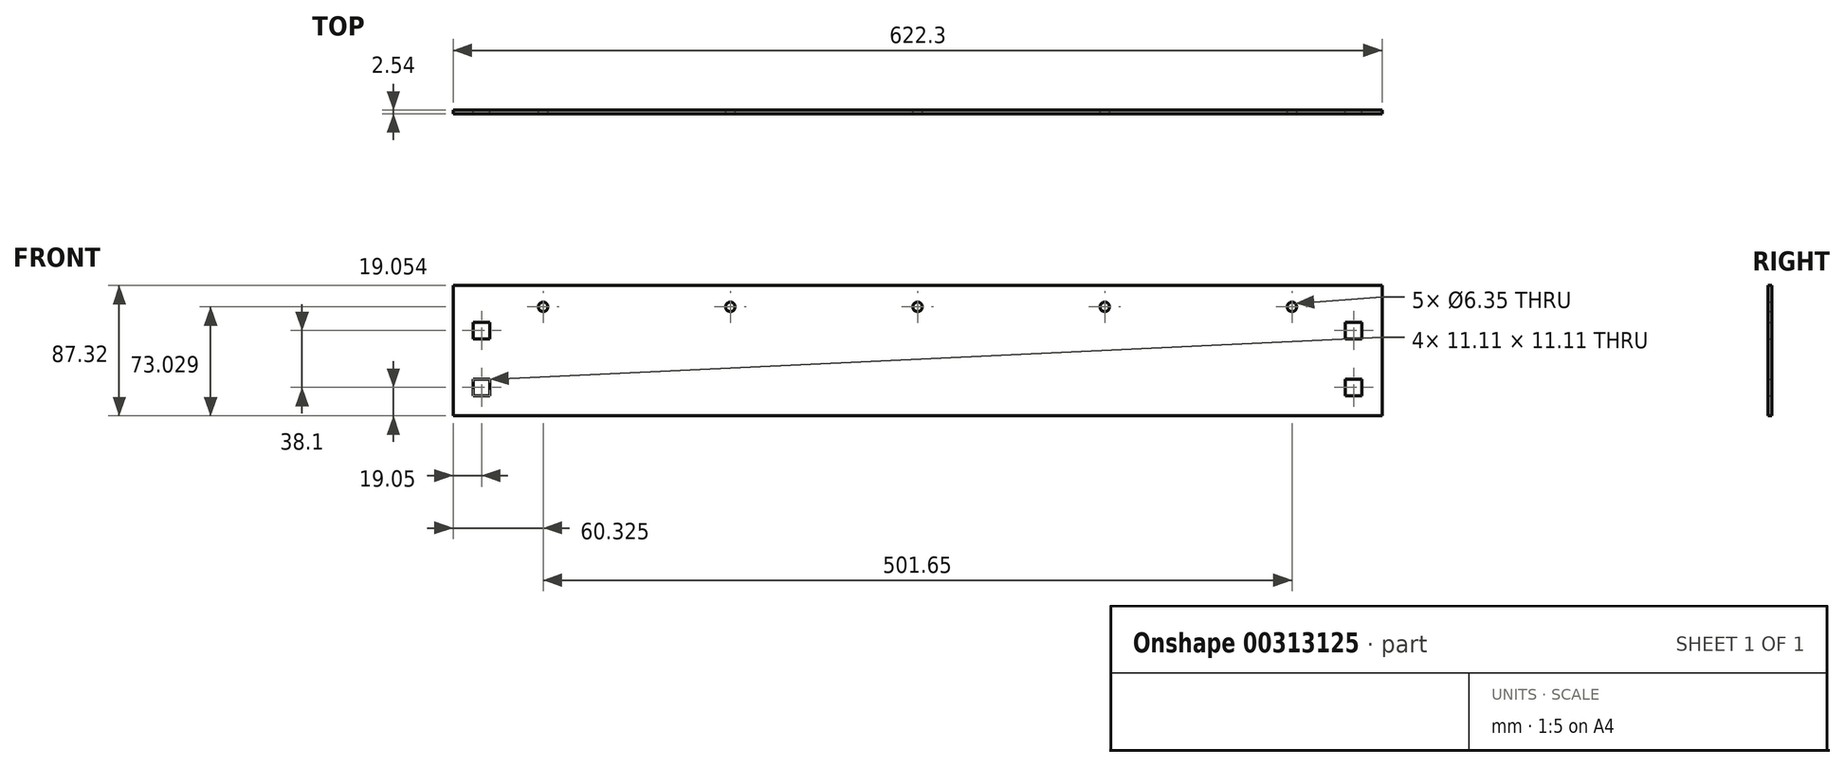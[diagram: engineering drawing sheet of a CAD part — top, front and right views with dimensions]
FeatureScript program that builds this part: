
annotation { "Feature Type Name" : "Feature", "Feature Type Description" : "" }
export const myFeature = defineFeature(function(context is Context, id is Id, definition is map)
    precondition{}
    {
        {
            var Q0;
            Q0=qCreatedBy(makeId("Front.planeOp"),FACE);
            var sketch = newSketch(context, id + "F0", { "sketchPlane" : qUnion([Q0])});
            skLineSegment(sketch, "E0.bottom", {"start": v(311.15, 43.66) * mm, "end": v(-311.15, 43.66) * mm});
            skLineSegment(sketch, "E0.top", {"start": v(311.15, -43.66) * mm, "end": v(-311.15, -43.66) * mm});
            skLineSegment(sketch, "E0.left", {"start": v(311.15, 43.66) * mm, "end": v(311.15, -43.66) * mm});
            skLineSegment(sketch, "E0.right", {"start": v(-311.15, 43.66) * mm, "end": v(-311.15, -43.66) * mm});
            skPoint(sketch, "E0.middle", {"position": v(0, 0) * mm});
            skLineSegment(sketch, "E1.bottom", {"start": v(-286.54, 7.94) * mm, "end": v(-297.66, 7.94) * mm});
            skLineSegment(sketch, "E1.top", {"start": v(-286.54, 19.05) * mm, "end": v(-297.66, 19.05) * mm});
            skLineSegment(sketch, "E1.left", {"start": v(-286.54, 7.94) * mm, "end": v(-286.54, 19.05) * mm});
            skLineSegment(sketch, "E1.right", {"start": v(-297.66, 7.94) * mm, "end": v(-297.66, 19.05) * mm});
            skPoint(sketch, "E1.middle", {"position": v(-292.1, 13.5) * mm});
            skLineSegment(sketch, "E2.bottom", {"start": v(-297.66, -30.16) * mm, "end": v(-286.54, -30.16) * mm});
            skLineSegment(sketch, "E2.top", {"start": v(-297.66, -19.05) * mm, "end": v(-286.54, -19.05) * mm});
            skLineSegment(sketch, "E2.left", {"start": v(-297.66, -30.16) * mm, "end": v(-297.66, -19.05) * mm});
            skLineSegment(sketch, "E2.right", {"start": v(-286.54, -30.16) * mm, "end": v(-286.54, -19.05) * mm});
            skPoint(sketch, "E2.middle", {"position": v(-292.1, -24.6) * mm});
            skPoint(sketch, "E3.1.0.0", {"position": v(292.1, -24.6) * mm});
            skPoint(sketch, "E3.1.0.1", {"position": v(292.1, 13.5) * mm});
            skLineSegment(sketch, "E3.1.0.2", {"start": v(286.54, 7.94) * mm, "end": v(286.54, 19.05) * mm});
            skLineSegment(sketch, "E3.1.0.3", {"start": v(297.66, 7.94) * mm, "end": v(297.66, 19.05) * mm});
            skLineSegment(sketch, "E3.1.0.4", {"start": v(297.66, 19.05) * mm, "end": v(286.54, 19.05) * mm});
            skLineSegment(sketch, "E3.1.0.5", {"start": v(297.66, 7.94) * mm, "end": v(286.54, 7.94) * mm});
            skLineSegment(sketch, "E3.1.0.6", {"start": v(286.54, -30.16) * mm, "end": v(297.66, -30.16) * mm});
            skLineSegment(sketch, "E3.1.0.7", {"start": v(286.54, -19.05) * mm, "end": v(297.66, -19.05) * mm});
            skLineSegment(sketch, "E3.1.0.8", {"start": v(286.54, -30.16) * mm, "end": v(286.54, -19.05) * mm});
            skLineSegment(sketch, "E3.1.0.9", {"start": v(297.66, -30.16) * mm, "end": v(297.66, -19.05) * mm});
            skLineSegment(sketch, "E3.direction1", {"start": v(-297.66, -30.16) * mm, "end": v(286.54, -30.16) * mm, "construction": true});
            skCircle(sketch, "E4", {"center": v(0, 29.37) * mm, "radius": 3.18 * mm});
            skPoint(sketch, "E4.centerSnap0", {"position": v(0, 43.66) * mm});
            skCircle(sketch, "E5", {"center": v(125.41, 29.37) * mm, "radius": 3.18 * mm});
            skCircle(sketch, "E6", {"center": v(250.83, 29.37) * mm, "radius": 3.18 * mm});
            skCircle(sketch, "E7", {"center": v(-125.41, 29.37) * mm, "radius": 3.18 * mm});
            skCircle(sketch, "E8", {"center": v(-250.83, 29.37) * mm, "radius": 3.18 * mm});
            skLineSegment(sketch, "E9", {"start": v(-250.83, 29.37) * mm, "end": v(0, 29.37) * mm, "construction": true});
            skLineSegment(sketch, "E10", {"start": v(0, 29.37) * mm, "end": v(250.83, 29.37) * mm, "construction": true});
            skSolve(sketch);
        }
        {
            var Q0;
            Q0=makeQuery(id+"F0.imprint","IMPRINT",FACE,{"disambiguationData":[TD([[makeQuery(id+"F0.imprint","IMPRINT",EDGE,{"derivedFrom":sQuery(id+"F0.wireOp",EDGE,"E0.bottom")}),1.0]])]});
            extrude(context, id + "F1", {"entities" : qUnion([Q0]), "endBound" : BoundingType.SYMMETRIC, "depth" : 2.54 * mm});
        }
    });
